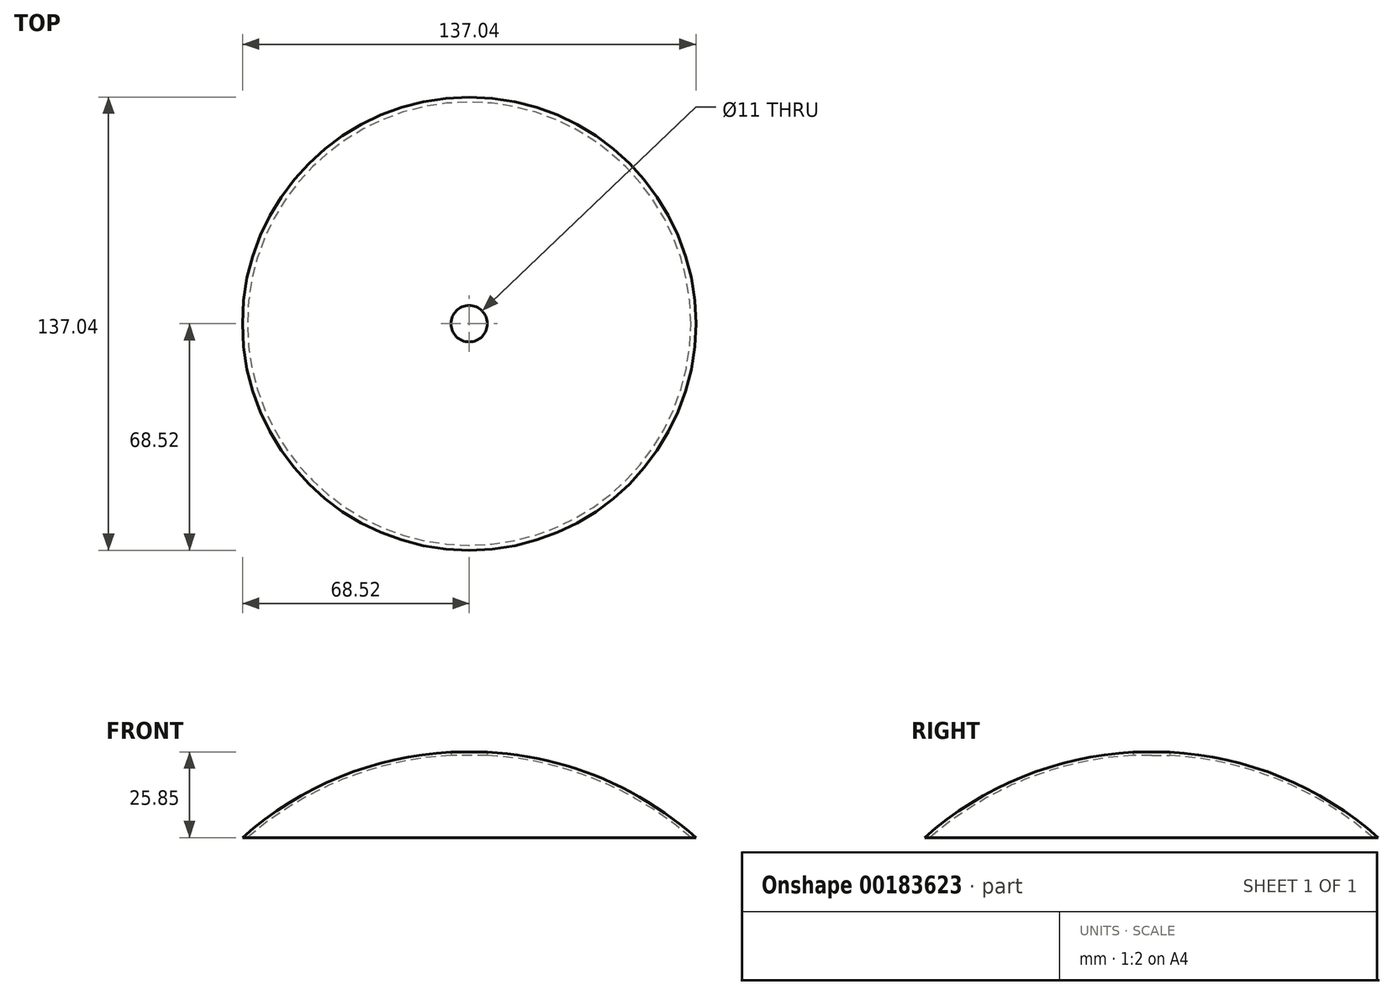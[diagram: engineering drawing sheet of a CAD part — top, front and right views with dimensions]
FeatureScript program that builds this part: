
annotation { "Feature Type Name" : "Feature", "Feature Type Description" : "" }
export const myFeature = defineFeature(function(context is Context, id is Id, definition is map)
    precondition{}
    {
        {
            var Q0;
            Q0=qCreatedBy(makeId("Front.planeOp"),FACE);
            var sketch = newSketch(context, id + "F0", { "sketchPlane" : qUnion([Q0])});
            skLineSegment(sketch, "E0.bottom", {"start": v(0, -12.5) * mm, "end": v(67, -12.5) * mm});
            skArc(sketch, "E1", {"start": v(67, -12.5) * mm, "mid": v(35.76, 6.05) * mm, "end": v(0, 12.5) * mm});
            skLineSegment(sketch, "E2", {"start": v(0, 12.5) * mm, "end": v(0, -12.5) * mm});
            skSolve(sketch);
        }
        {
            var Q0;
            Q0 = qSketchRegion(id + "F0", true);
            var Q1;
            Q1=sQuery(id+"F0.wireOp",EDGE,"E2");
            revolve(context, id + "F1", {"entities" : qUnion([Q0]), "axis" : qUnion([Q1]), "revolveType" : RevolveType.FULL});
        }
        {
            var Q0;
            Q0=makeQuery(id+"F1.opRevolve","SWEPT_FACE",FACE,{"disambiguationData":[OSD([sQuery(id+"F0.wireOp",EDGE,"E0.bottom")])]});
            shell(context, id + "F2", {"entities" : qUnion([Q0]), "thickness" : 1 * mm, "oppositeDirection" : true});
        }
        {
            var Q0;
            Q0=qCreatedBy(makeId("Top.planeOp"),FACE);
            var sketch = newSketch(context, id + "F3", { "sketchPlane" : qUnion([Q0])});
            skCircle(sketch, "E3", {"center": v(0, 0) * mm, "radius": 5.5 * mm});
            skSolve(sketch);
        }
        {
            var Q0;
            Q0 = qSketchRegion(id + "F3", true);
            extrude(context, id + "F4", {"entities" : qUnion([Q0]), "operationType" : NewBodyOperationType.REMOVE, "endBound" : BoundingType.THROUGH_ALL, "depth" : 25 * mm});
        }
    });
